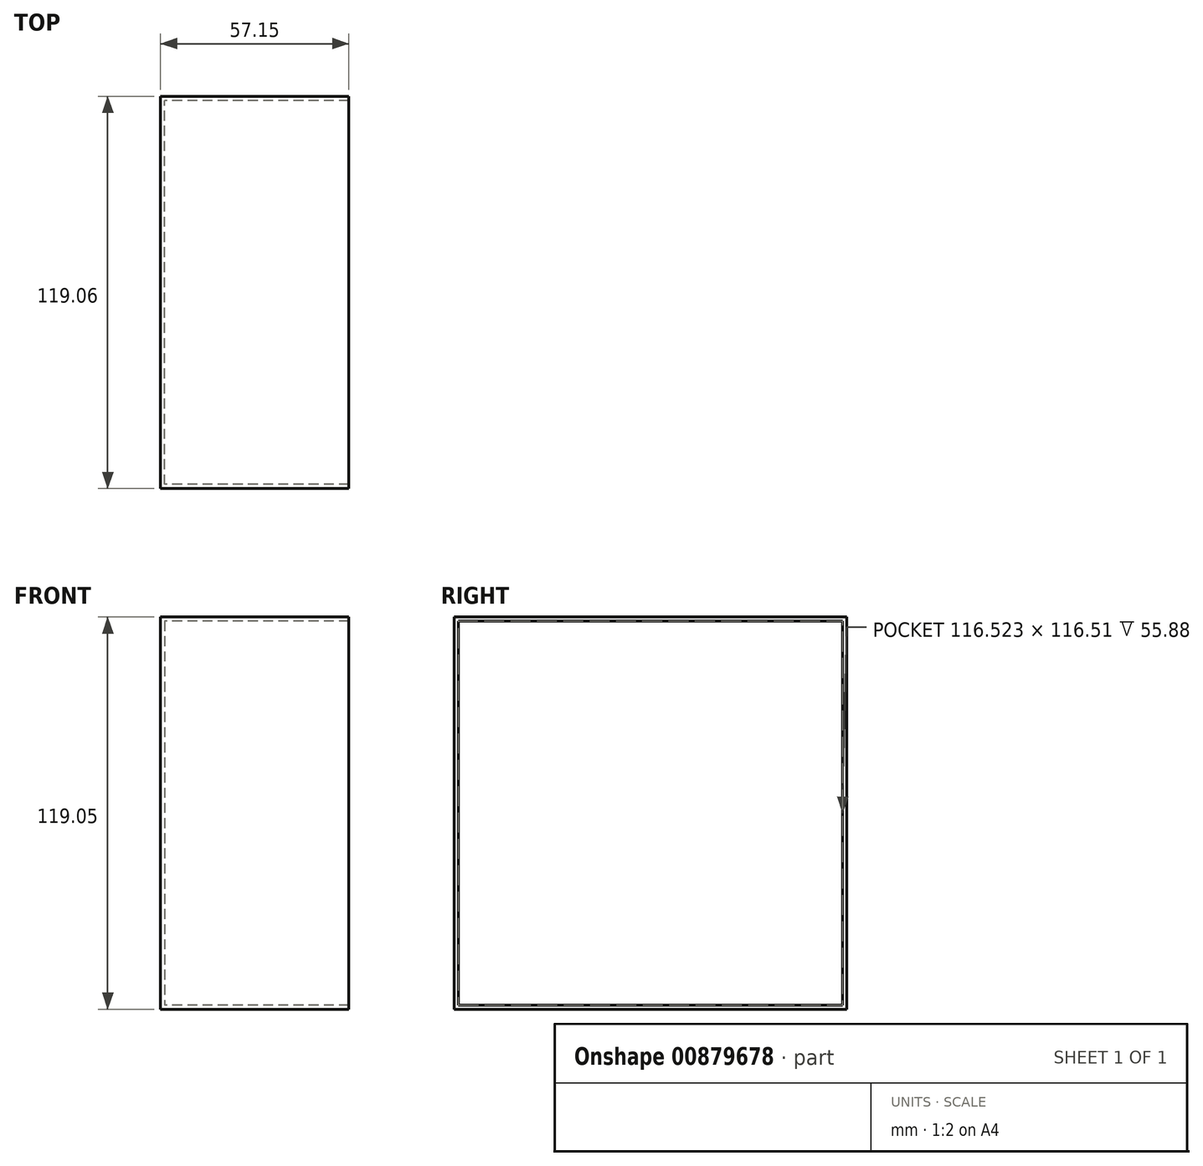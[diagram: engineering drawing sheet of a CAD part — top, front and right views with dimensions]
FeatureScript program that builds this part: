
annotation { "Feature Type Name" : "Feature", "Feature Type Description" : "" }
export const myFeature = defineFeature(function(context is Context, id is Id, definition is map)
    precondition{}
    {
        {
            var Q0;
            Q0=qCreatedBy(makeId("Right.planeOp"),FACE);
            var sketch = newSketch(context, id + "F0", { "sketchPlane" : qUnion([Q0])});
            skLineSegment(sketch, "E0.bottom", {"start": v(-56.83, 45.72) * mm, "end": v(62.23, 45.72) * mm});
            skLineSegment(sketch, "E0.top", {"start": v(-56.83, -73.33) * mm, "end": v(62.23, -73.33) * mm});
            skLineSegment(sketch, "E0.left", {"start": v(-56.83, 45.72) * mm, "end": v(-56.83, -73.33) * mm});
            skLineSegment(sketch, "E0.right", {"start": v(62.23, 45.72) * mm, "end": v(62.23, -73.33) * mm});
            skSolve(sketch);
        }
        {
            var Q0;
            Q0=makeQuery(id+"F0.imprint","IMPRINT",FACE,{"disambiguationData":[TD([[makeQuery(id+"F0.imprint","IMPRINT",EDGE,{"derivedFrom":sQuery(id+"F0.wireOp",EDGE,"E0.bottom")}),-1.0]])]});
            extrude(context, id + "F1", {"entities" : qUnion([Q0]), "depth" : 57.15 * mm, "offsetDistance" : 25.4 * mm});
        }
        {
            var Q0;
            Q0=makeQuery(id+"F1.opExtrude","CAP_FACE",FACE,{"disambiguationData":[OSD([sQuery(id+"F0.wireOp",EDGE,"E0.bottom"),sQuery(id+"F0.wireOp",EDGE,"E0.top"),sQuery(id+"F0.wireOp",EDGE,"E0.left"),sQuery(id+"F0.wireOp",EDGE,"E0.right")])],"isStart":false});
            shell(context, id + "F2", {"entities" : qUnion([Q0]), "thickness" : 1.27 * mm});
        }
    });
